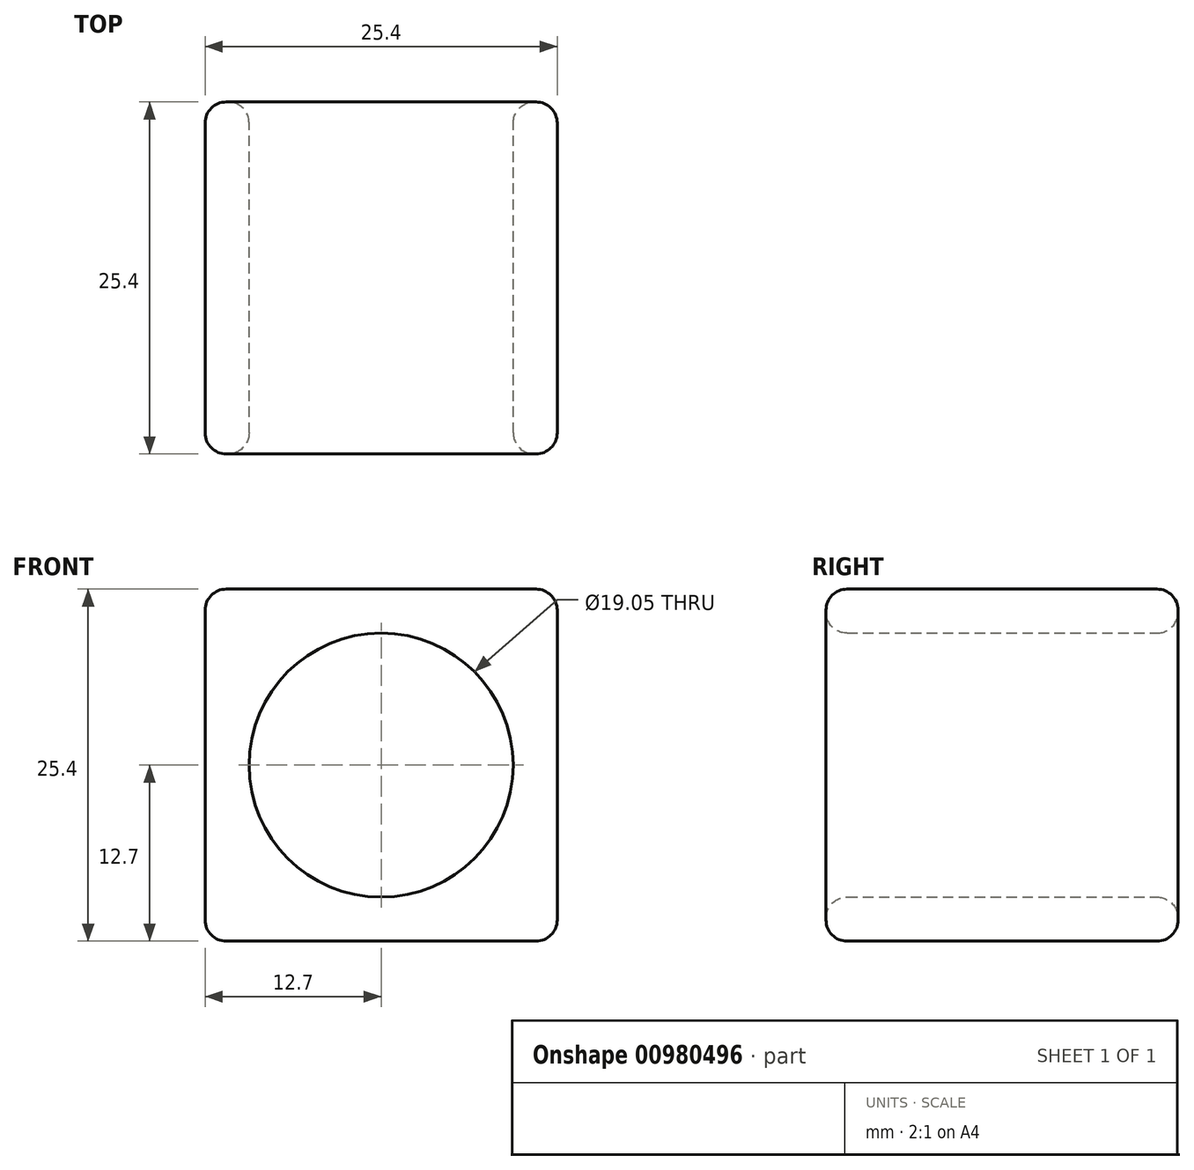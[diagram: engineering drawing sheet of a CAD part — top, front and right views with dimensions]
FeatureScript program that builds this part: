
annotation { "Feature Type Name" : "Feature", "Feature Type Description" : "" }
export const myFeature = defineFeature(function(context is Context, id is Id, definition is map)
    precondition{}
    {
        {
            var Q0;
            Q0=qCreatedBy(makeId("Front.planeOp"),FACE);
            var sketch = newSketch(context, id + "F0", { "sketchPlane" : qUnion([Q0])});
            skLineSegment(sketch, "E0.bottom", {"start": v(12.7, -12.7) * mm, "end": v(-12.7, -12.7) * mm});
            skLineSegment(sketch, "E0.top", {"start": v(12.7, 12.7) * mm, "end": v(-12.7, 12.7) * mm});
            skLineSegment(sketch, "E0.left", {"start": v(12.7, -12.7) * mm, "end": v(12.7, 12.7) * mm});
            skLineSegment(sketch, "E0.right", {"start": v(-12.7, -12.7) * mm, "end": v(-12.7, 12.7) * mm});
            skPoint(sketch, "E0.middle", {"position": v(0, 0) * mm});
            skCircle(sketch, "E1", {"center": v(0, 0) * mm, "radius": 9.53 * mm});
            skSolve(sketch);
        }
        {
            var Q0;
            Q0 = qSketchRegion(id + "F0", true);
            extrude(context, id + "F1", {"entities" : qUnion([Q0]), "depth" : 25.4 * mm, "offsetDistance" : 25.4 * mm});
        }
        {
            var Q0;
            Q0=makeQuery(id+"F1.opExtrude","CAP_EDGE",EDGE,{"disambiguationData":[OSD([sQuery(id+"F0.wireOp",EDGE,"E1")])],"isStart":false});
            var Q1;
            Q1=makeQuery(id+"F1.opExtrude","SWEPT_EDGE",EDGE,{"disambiguationData":[OSD([sQuery(id+"F0.wireOp",EDGE,"E0.bottom"),sQuery(id+"F0.wireOp",EDGE,"E0.left")])]});
            var Q2;
            Q2=makeQuery(id+"F1.opExtrude","SWEPT_EDGE",EDGE,{"disambiguationData":[OSD([sQuery(id+"F0.wireOp",EDGE,"E0.top"),sQuery(id+"F0.wireOp",EDGE,"E0.left")])]});
            var Q3;
            Q3=makeQuery(id+"F1.opExtrude","SWEPT_EDGE",EDGE,{"disambiguationData":[OSD([sQuery(id+"F0.wireOp",EDGE,"E0.top"),sQuery(id+"F0.wireOp",EDGE,"E0.right")])]});
            var Q4;
            Q4=makeQuery(id+"F1.opExtrude","CAP_EDGE",EDGE,{"disambiguationData":[OSD([sQuery(id+"F0.wireOp",EDGE,"E0.bottom")])],"isStart":false});
            var Q5;
            Q5=makeQuery(id+"F1.opExtrude","CAP_EDGE",EDGE,{"disambiguationData":[OSD([sQuery(id+"F0.wireOp",EDGE,"E0.top")])],"isStart":true});
            var Q6;
            Q6=makeQuery(id+"F1.opExtrude","CAP_EDGE",EDGE,{"disambiguationData":[OSD([sQuery(id+"F0.wireOp",EDGE,"E0.top")])],"isStart":false});
            var Q7;
            Q7=makeQuery(id+"F1.opExtrude","CAP_EDGE",EDGE,{"disambiguationData":[OSD([sQuery(id+"F0.wireOp",EDGE,"E0.left")])],"isStart":true});
            var Q8;
            Q8=makeQuery(id+"F1.opExtrude","CAP_EDGE",EDGE,{"disambiguationData":[OSD([sQuery(id+"F0.wireOp",EDGE,"E0.left")])],"isStart":false});
            var Q9;
            Q9=makeQuery(id+"F1.opExtrude","CAP_EDGE",EDGE,{"disambiguationData":[OSD([sQuery(id+"F0.wireOp",EDGE,"E0.right")])],"isStart":false});
            var Q10;
            Q10=makeQuery(id+"F1.opExtrude","CAP_EDGE",EDGE,{"disambiguationData":[OSD([sQuery(id+"F0.wireOp",EDGE,"E1")])],"isStart":true});
            var Q11;
            Q11=makeQuery(id+"F1.opExtrude","SWEPT_EDGE",EDGE,{"disambiguationData":[OSD([sQuery(id+"F0.wireOp",EDGE,"E0.bottom"),sQuery(id+"F0.wireOp",EDGE,"E0.right")])]});
            var Q12;
            Q12=makeQuery(id+"F1.opExtrude","CAP_EDGE",EDGE,{"disambiguationData":[OSD([sQuery(id+"F0.wireOp",EDGE,"E0.bottom")])],"isStart":true});
            var Q13;
            Q13=makeQuery(id+"F1.opExtrude","CAP_EDGE",EDGE,{"disambiguationData":[OSD([sQuery(id+"F0.wireOp",EDGE,"E0.right")])],"isStart":true});
            fillet(context, id + "F2", {"entities" : qUnion([Q0, Q1, Q2, Q3, Q4, Q5, Q6, Q7, Q8, Q9, Q10, Q11, Q12, Q13]), "radius" : 1.52 * mm, "tangentPropagation" : true, "allowEdgeOverflow" : false});
        }
    });
